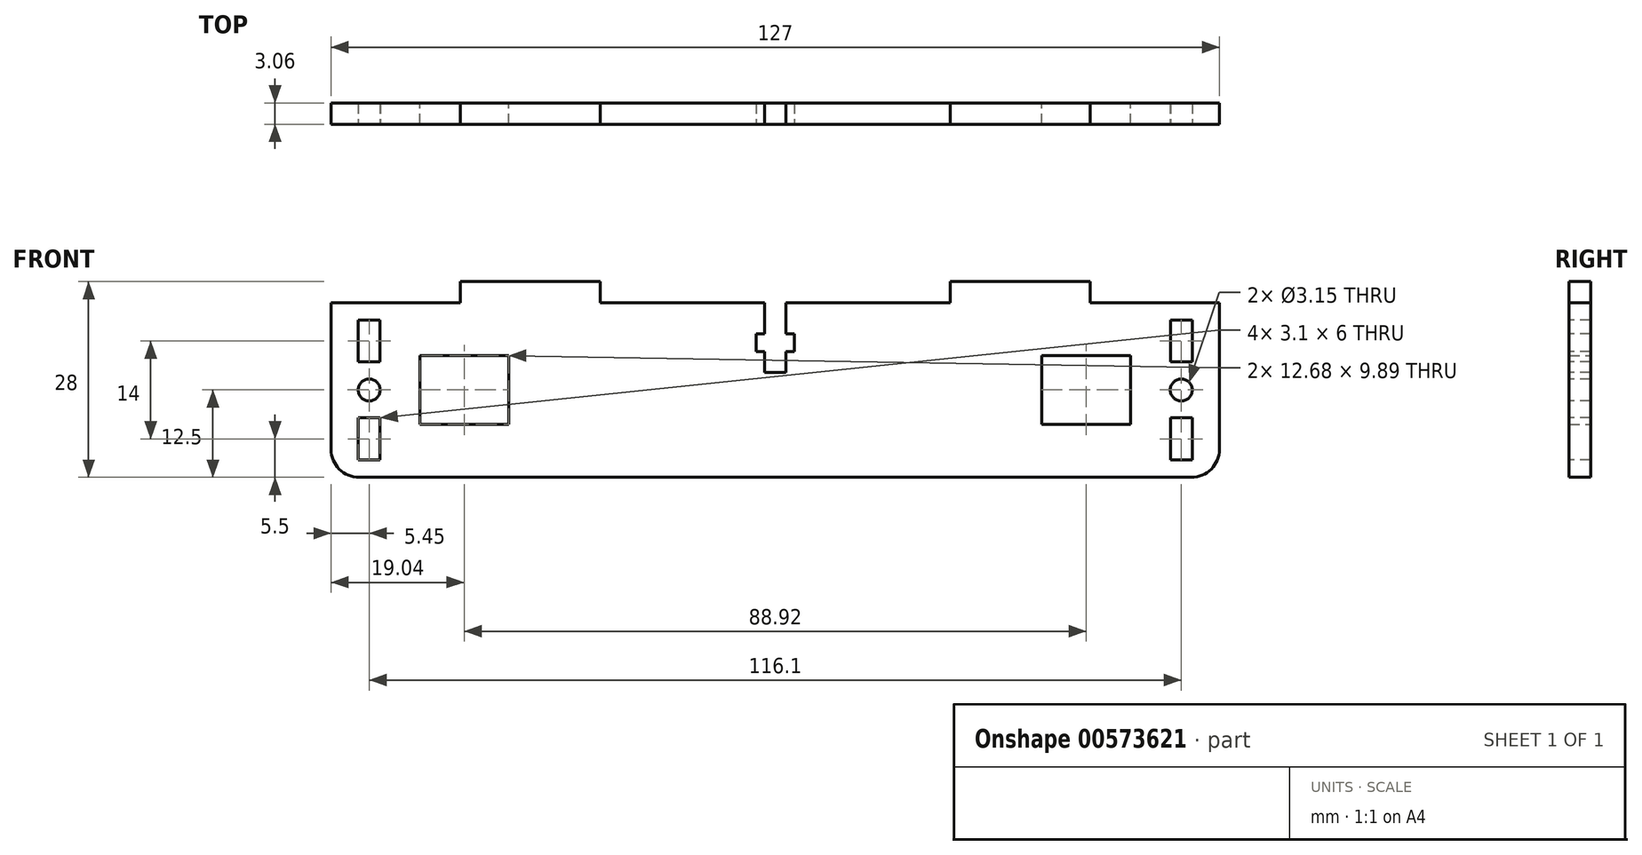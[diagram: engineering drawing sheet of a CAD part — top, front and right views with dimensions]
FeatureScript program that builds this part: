
annotation { "Feature Type Name" : "Feature", "Feature Type Description" : "" }
export const myFeature = defineFeature(function(context is Context, id is Id, definition is map)
    precondition{}
    {
        {
            var Q0;
            Q0=qCreatedBy(makeId("Front.planeOp"),FACE);
            var sketch = newSketch(context, id + "F0", { "sketchPlane" : qUnion([Q0])});
            skLineSegment(sketch, "E0.bottom", {"start": v(63.5, -12.5) * mm, "end": v(-63.5, -12.5) * mm});
            skLineSegment(sketch, "E0.top", {"start": v(63.5, 12.5) * mm, "end": v(-63.5, 12.5) * mm});
            skLineSegment(sketch, "E0.left", {"start": v(63.5, -12.5) * mm, "end": v(63.5, 12.5) * mm});
            skLineSegment(sketch, "E0.right", {"start": v(-63.5, -12.5) * mm, "end": v(-63.5, 12.5) * mm});
            skPoint(sketch, "E0.middle", {"position": v(0, 0) * mm});
            skLineSegment(sketch, "E1.bottom", {"start": v(-38.12, -4.95) * mm, "end": v(-50.8, -4.95) * mm});
            skLineSegment(sketch, "E1.top", {"start": v(-38.12, 4.94) * mm, "end": v(-50.8, 4.94) * mm});
            skLineSegment(sketch, "E1.left", {"start": v(-38.12, -4.95) * mm, "end": v(-38.12, 4.94) * mm});
            skLineSegment(sketch, "E1.right", {"start": v(-50.8, -4.95) * mm, "end": v(-50.8, 4.94) * mm});
            skPoint(sketch, "E1.middle", {"position": v(-44.46, 0) * mm});
            skLineSegment(sketch, "E2", {"start": v(0, 12.5) * mm, "end": v(0, -12.5) * mm, "construction": true});
            skLineSegment(sketch, "E3.MirrorCS", {"start": v(38.12, -4.95) * mm, "end": v(38.12, 4.95) * mm});
            skLineSegment(sketch, "E4.MirrorCS", {"start": v(38.12, 4.94) * mm, "end": v(50.8, 4.94) * mm});
            skLineSegment(sketch, "E5.MirrorCS", {"start": v(38.12, -4.95) * mm, "end": v(50.8, -4.95) * mm});
            skLineSegment(sketch, "E6.MirrorCS", {"start": v(50.8, -4.94) * mm, "end": v(50.8, 4.95) * mm});
            skPoint(sketch, "E7.MirrorP", {"position": v(44.46, 0) * mm});
            skSolve(sketch);
        }
        {
            var Q0;
            Q0 = qSketchRegion(id + "F0", true);
            extrude(context, id + "F1", {"entities" : qUnion([Q0]), "endBound" : BoundingType.SYMMETRIC, "depth" : 3.05 * mm, "offsetDistance" : 25 * mm});
        }
        {
            var Q0;
            Q0=makeQuery(id+"F1.opExtrude","CAP_FACE",FACE,{"disambiguationData":[OSD([sQuery(id+"F0.wireOp",EDGE,"E0.bottom"),sQuery(id+"F0.wireOp",EDGE,"E0.top"),sQuery(id+"F0.wireOp",EDGE,"E0.left"),sQuery(id+"F0.wireOp",EDGE,"E0.right"),sQuery(id+"F0.wireOp",EDGE,"E1.bottom"),sQuery(id+"F0.wireOp",EDGE,"E1.top"),sQuery(id+"F0.wireOp",EDGE,"E1.left"),sQuery(id+"F0.wireOp",EDGE,"E1.right"),sQuery(id+"F0.wireOp",EDGE,"E3.MirrorCS"),sQuery(id+"F0.wireOp",EDGE,"E4.MirrorCS"),sQuery(id+"F0.wireOp",EDGE,"E5.MirrorCS"),sQuery(id+"F0.wireOp",EDGE,"E6.MirrorCS")])],"isStart":false});
            var sketch = newSketch(context, id + "F2", { "sketchPlane" : qUnion([Q0])});
            skLineSegment(sketch, "E8", {"start": v(0, 12.5) * mm, "end": v(0, -12.5) * mm, "construction": true});
            skLineSegment(sketch, "E9.bottom", {"start": v(-45, 12.5) * mm, "end": v(-25, 12.5) * mm});
            skLineSegment(sketch, "E9.top", {"start": v(-45, 15.5) * mm, "end": v(-25, 15.5) * mm});
            skLineSegment(sketch, "E9.left", {"start": v(-45, 12.5) * mm, "end": v(-45, 15.5) * mm});
            skLineSegment(sketch, "E9.right", {"start": v(-25, 12.5) * mm, "end": v(-25, 15.5) * mm});
            skLineSegment(sketch, "E10.MirrorCS", {"start": v(25, 12.5) * mm, "end": v(25, 15.5) * mm});
            skLineSegment(sketch, "E11.MirrorCS", {"start": v(45, 12.5) * mm, "end": v(45, 15.5) * mm});
            skLineSegment(sketch, "E12.MirrorCS", {"start": v(45, 12.5) * mm, "end": v(25, 12.5) * mm});
            skLineSegment(sketch, "E13.MirrorCS", {"start": v(45, 15.5) * mm, "end": v(25, 15.5) * mm});
            skSolve(sketch);
        }
        {
            var Q0;
            Q0 = qSketchRegion(id + "F2", true);
            var Q1;
            Q1=makeQuery(id+"F1.opExtrude","CAP_FACE",FACE,{"disambiguationData":[OSD([sQuery(id+"F0.wireOp",EDGE,"E0.bottom"),sQuery(id+"F0.wireOp",EDGE,"E0.top"),sQuery(id+"F0.wireOp",EDGE,"E0.left"),sQuery(id+"F0.wireOp",EDGE,"E0.right"),sQuery(id+"F0.wireOp",EDGE,"E1.bottom"),sQuery(id+"F0.wireOp",EDGE,"E1.top"),sQuery(id+"F0.wireOp",EDGE,"E1.left"),sQuery(id+"F0.wireOp",EDGE,"E1.right"),sQuery(id+"F0.wireOp",EDGE,"E3.MirrorCS"),sQuery(id+"F0.wireOp",EDGE,"E4.MirrorCS"),sQuery(id+"F0.wireOp",EDGE,"E5.MirrorCS"),sQuery(id+"F0.wireOp",EDGE,"E6.MirrorCS")])],"isStart":true});
            extrude(context, id + "F3", {"entities" : qUnion([Q0]), "operationType" : NewBodyOperationType.ADD, "endBound" : BoundingType.UP_TO_SURFACE, "oppositeDirection" : true, "depth" : 25 * mm, "endBoundEntityFace" : qUnion([Q1]), "offsetDistance" : 25 * mm});
        }
        {
            var Q0;
            Q0=makeQuery(id+"F3.boolean.opBoolean","MERGE",FACE,{"derivedFrom":[makeQuery(id+"F1.opExtrude","CAP_FACE",FACE,{"disambiguationData":[OSD([sQuery(id+"F0.wireOp",EDGE,"E0.bottom"),sQuery(id+"F0.wireOp",EDGE,"E0.top"),sQuery(id+"F0.wireOp",EDGE,"E0.left"),sQuery(id+"F0.wireOp",EDGE,"E0.right"),sQuery(id+"F0.wireOp",EDGE,"E1.bottom"),sQuery(id+"F0.wireOp",EDGE,"E1.top"),sQuery(id+"F0.wireOp",EDGE,"E1.left"),sQuery(id+"F0.wireOp",EDGE,"E1.right"),sQuery(id+"F0.wireOp",EDGE,"E3.MirrorCS"),sQuery(id+"F0.wireOp",EDGE,"E4.MirrorCS"),sQuery(id+"F0.wireOp",EDGE,"E5.MirrorCS"),sQuery(id+"F0.wireOp",EDGE,"E6.MirrorCS")])],"isStart":false}),makeQuery(id+"F3.opExtrude","CAP_FACE",FACE,{"disambiguationData":[OSD([sQuery(id+"F2.wireOp",EDGE,"E9.bottom"),sQuery(id+"F2.wireOp",EDGE,"E9.top"),sQuery(id+"F2.wireOp",EDGE,"E9.left"),sQuery(id+"F2.wireOp",EDGE,"E9.right")])],"isStart":true}),makeQuery(id+"F3.opExtrude","CAP_FACE",FACE,{"disambiguationData":[OSD([sQuery(id+"F2.wireOp",EDGE,"E10.MirrorCS"),sQuery(id+"F2.wireOp",EDGE,"E11.MirrorCS"),sQuery(id+"F2.wireOp",EDGE,"E12.MirrorCS"),sQuery(id+"F2.wireOp",EDGE,"E13.MirrorCS")])],"isStart":true})]});
            var sketch = newSketch(context, id + "F4", { "sketchPlane" : qUnion([Q0])});
            skLineSegment(sketch, "E14.bottom", {"start": v(-1.55, 12.5) * mm, "end": v(1.55, 12.5) * mm});
            skLineSegment(sketch, "E14.top", {"start": v(-1.55, 2.5) * mm, "end": v(1.55, 2.5) * mm});
            skLineSegment(sketch, "E14.left", {"start": v(-1.55, 12.5) * mm, "end": v(-1.55, 2.5) * mm});
            skLineSegment(sketch, "E14.right", {"start": v(1.55, 12.5) * mm, "end": v(1.55, 2.5) * mm});
            skLineSegment(sketch, "E15", {"start": v(0, 12.5) * mm, "end": v(0, -12.5) * mm, "construction": true});
            skPoint(sketch, "E16", {"position": v(0, 2.5) * mm});
            skLineSegment(sketch, "E17", {"start": v(0, 12.5) * mm, "end": v(0, 2.5) * mm, "construction": true});
            skLineSegment(sketch, "E18.bottom", {"start": v(2.7, 5.5) * mm, "end": v(-2.7, 5.5) * mm});
            skLineSegment(sketch, "E18.top", {"start": v(2.7, 8) * mm, "end": v(-2.7, 8) * mm});
            skLineSegment(sketch, "E18.left", {"start": v(2.7, 5.5) * mm, "end": v(2.7, 8) * mm});
            skLineSegment(sketch, "E18.right", {"start": v(-2.7, 5.5) * mm, "end": v(-2.7, 8) * mm});
            skPoint(sketch, "E18.middle", {"position": v(0, 6.75) * mm});
            skSolve(sketch);
        }
        {
            var Q0;
            Q0 = qSketchRegion(id + "F4", true);
            extrude(context, id + "F5", {"entities" : qUnion([Q0]), "operationType" : NewBodyOperationType.REMOVE, "endBound" : BoundingType.UP_TO_NEXT, "oppositeDirection" : true, "depth" : 25 * mm, "offsetDistance" : 25 * mm});
        }
        {
            var Q0;
            Q0=makeQuery(id+"F3.boolean.opBoolean","MERGE",FACE,{"derivedFrom":[makeQuery(id+"F1.opExtrude","CAP_FACE",FACE,{"disambiguationData":[OSD([sQuery(id+"F0.wireOp",EDGE,"E0.bottom"),sQuery(id+"F0.wireOp",EDGE,"E0.top"),sQuery(id+"F0.wireOp",EDGE,"E0.left"),sQuery(id+"F0.wireOp",EDGE,"E0.right"),sQuery(id+"F0.wireOp",EDGE,"E1.bottom"),sQuery(id+"F0.wireOp",EDGE,"E1.top"),sQuery(id+"F0.wireOp",EDGE,"E1.left"),sQuery(id+"F0.wireOp",EDGE,"E1.right"),sQuery(id+"F0.wireOp",EDGE,"E3.MirrorCS"),sQuery(id+"F0.wireOp",EDGE,"E4.MirrorCS"),sQuery(id+"F0.wireOp",EDGE,"E5.MirrorCS"),sQuery(id+"F0.wireOp",EDGE,"E6.MirrorCS")])],"isStart":false}),makeQuery(id+"F3.opExtrude","CAP_FACE",FACE,{"disambiguationData":[OSD([sQuery(id+"F2.wireOp",EDGE,"E9.bottom"),sQuery(id+"F2.wireOp",EDGE,"E9.top"),sQuery(id+"F2.wireOp",EDGE,"E9.left"),sQuery(id+"F2.wireOp",EDGE,"E9.right")])],"isStart":true}),makeQuery(id+"F3.opExtrude","CAP_FACE",FACE,{"disambiguationData":[OSD([sQuery(id+"F2.wireOp",EDGE,"E10.MirrorCS"),sQuery(id+"F2.wireOp",EDGE,"E11.MirrorCS"),sQuery(id+"F2.wireOp",EDGE,"E12.MirrorCS"),sQuery(id+"F2.wireOp",EDGE,"E13.MirrorCS")])],"isStart":true})]});
            var sketch = newSketch(context, id + "F6", { "sketchPlane" : qUnion([Q0])});
            skLineSegment(sketch, "E19", {"start": v(0, -12.5) * mm, "end": v(0, 2.5) * mm, "construction": true});
            skLineSegment(sketch, "E20", {"start": v(-58.05, 12.5) * mm, "end": v(-58.05, -12.5) * mm, "construction": true});
            skLineSegment(sketch, "E21.bottom", {"start": v(-56.5, 4) * mm, "end": v(-59.6, 4) * mm});
            skLineSegment(sketch, "E21.top", {"start": v(-56.5, 10) * mm, "end": v(-59.6, 10) * mm});
            skLineSegment(sketch, "E21.left", {"start": v(-56.5, 4) * mm, "end": v(-56.5, 10) * mm});
            skLineSegment(sketch, "E21.right", {"start": v(-59.6, 4) * mm, "end": v(-59.6, 10) * mm});
            skPoint(sketch, "E21.middle", {"position": v(-58.05, 7) * mm});
            skLineSegment(sketch, "E22", {"start": v(-63.5, 0) * mm, "end": v(0, 0) * mm, "construction": true});
            skPoint(sketch, "E23.MirrorP", {"position": v(-58.05, -7) * mm});
            skLineSegment(sketch, "E24.MirrorCS", {"start": v(-56.5, -4) * mm, "end": v(-59.6, -4) * mm});
            skLineSegment(sketch, "E25.MirrorCS", {"start": v(-59.6, -4) * mm, "end": v(-59.6, -10) * mm});
            skLineSegment(sketch, "E26.MirrorCS", {"start": v(-56.5, -4) * mm, "end": v(-56.5, -10) * mm});
            skLineSegment(sketch, "E27.MirrorCS", {"start": v(-56.5, -10) * mm, "end": v(-59.6, -10) * mm});
            skCircle(sketch, "E28", {"center": v(-58.05, 0) * mm, "radius": 1.57 * mm});
            skLineSegment(sketch, "E29.MirrorCS", {"start": v(56.5, 4) * mm, "end": v(59.6, 4) * mm});
            skPoint(sketch, "E30.MirrorP", {"position": v(58.05, -7) * mm});
            skPoint(sketch, "E31.MirrorP", {"position": v(58.05, 7) * mm});
            skLineSegment(sketch, "E32.MirrorCS", {"start": v(56.5, 10) * mm, "end": v(59.6, 10) * mm});
            skLineSegment(sketch, "E33.MirrorCS", {"start": v(56.5, 4) * mm, "end": v(56.5, 10) * mm});
            skLineSegment(sketch, "E34.MirrorCS", {"start": v(59.6, 4) * mm, "end": v(59.6, 10) * mm});
            skLineSegment(sketch, "E35.MirrorCS", {"start": v(56.5, -4) * mm, "end": v(59.6, -4) * mm});
            skLineSegment(sketch, "E36.MirrorCS", {"start": v(59.6, -4) * mm, "end": v(59.6, -10) * mm});
            skCircle(sketch, "E37.MirrorC", {"center": v(58.05, 0) * mm, "radius": 1.57 * mm});
            skLineSegment(sketch, "E38.MirrorCS", {"start": v(56.5, -10) * mm, "end": v(59.6, -10) * mm});
            skLineSegment(sketch, "E39.MirrorCS", {"start": v(56.5, -4) * mm, "end": v(56.5, -10) * mm});
            skSolve(sketch);
        }
        {
            var Q0;
            Q0 = qSketchRegion(id + "F6", true);
            extrude(context, id + "F7", {"entities" : qUnion([Q0]), "operationType" : NewBodyOperationType.REMOVE, "endBound" : BoundingType.UP_TO_NEXT, "oppositeDirection" : true, "depth" : 25 * mm, "offsetDistance" : 25 * mm});
        }
        {
            var Q0;
            Q0=makeQuery(id+"F1.opExtrude","SWEPT_EDGE",EDGE,{"disambiguationData":[OSD([sQuery(id+"F0.wireOp",EDGE,"E0.bottom"),sQuery(id+"F0.wireOp",EDGE,"E0.right")])]});
            var Q1;
            Q1=makeQuery(id+"F1.opExtrude","SWEPT_EDGE",EDGE,{"disambiguationData":[OSD([sQuery(id+"F0.wireOp",EDGE,"E0.bottom"),sQuery(id+"F0.wireOp",EDGE,"E0.left")])]});
            fillet(context, id + "F8", {"entities" : qUnion([Q0, Q1]), "radius" : 4 * mm, "tangentPropagation" : true, "allowEdgeOverflow" : false});
        }
    });
